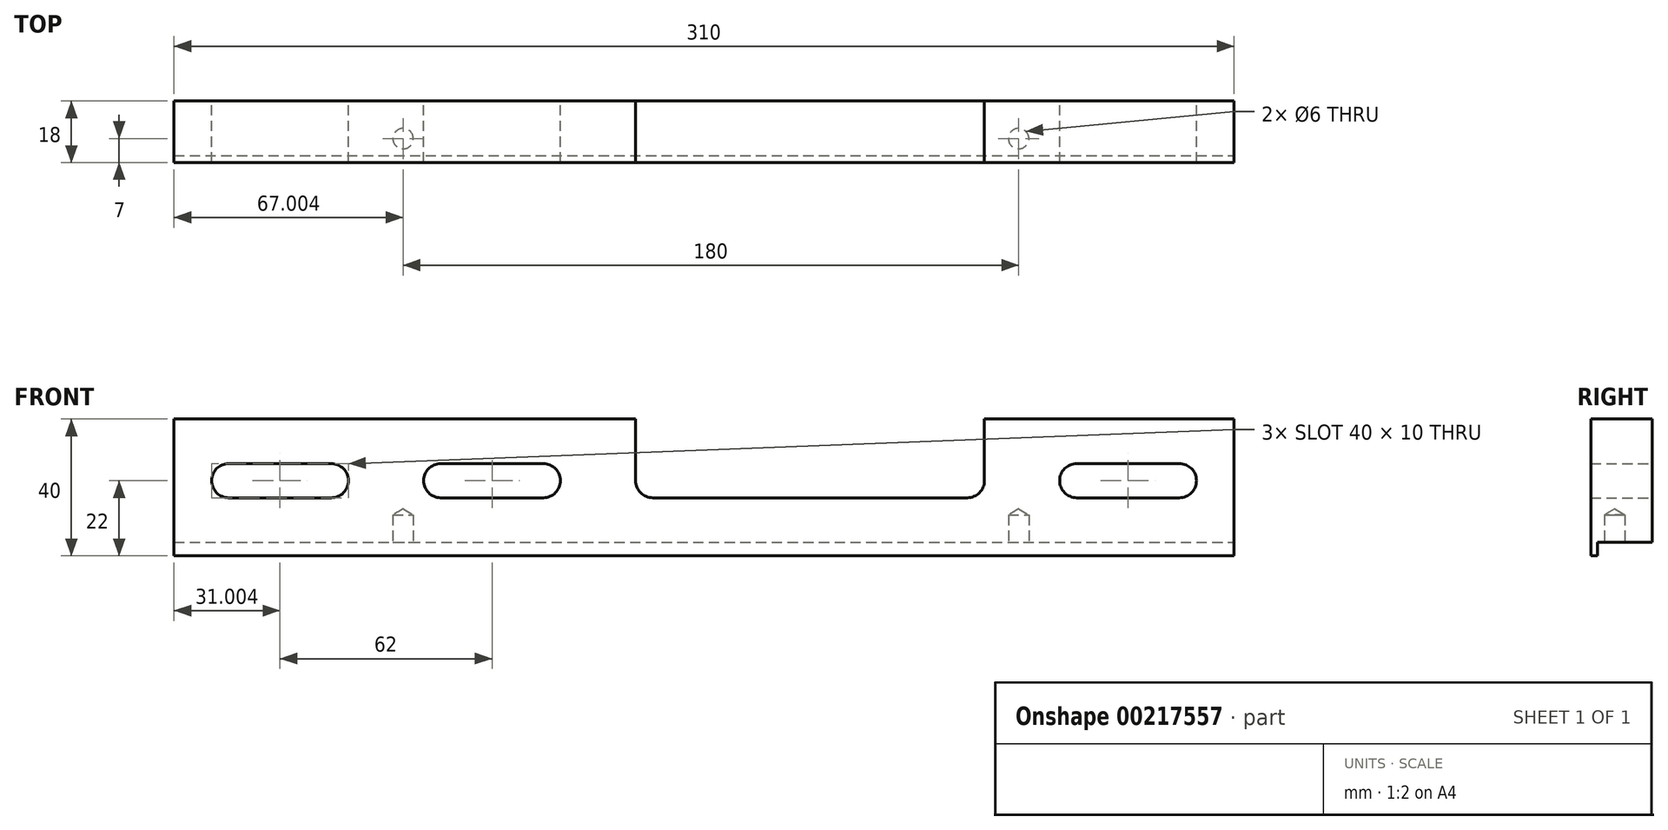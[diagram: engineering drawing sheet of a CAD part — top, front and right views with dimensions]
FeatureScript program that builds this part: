
annotation { "Feature Type Name" : "Feature", "Feature Type Description" : "" }
export const myFeature = defineFeature(function(context is Context, id is Id, definition is map)
    precondition{}
    {
        {
            var Q0;
            Q0=qCreatedBy(makeId("Front.planeOp"),FACE);
            var sketch = newSketch(context, id + "F0", { "sketchPlane" : qUnion([Q0])});
            skPoint(sketch, "E0.endSnap0", {"position": v(-230.99, 42.91) * mm});
            skLineSegment(sketch, "E1", {"start": v(-179.99, 20.91) * mm, "end": v(-489.99, 20.91) * mm});
            skLineSegment(sketch, "E2", {"start": v(-179.99, 20.91) * mm, "end": v(-179.99, 60.91) * mm});
            skLineSegment(sketch, "E3", {"start": v(-179.99, 60.91) * mm, "end": v(-252.99, 60.91) * mm});
            skLineSegment(sketch, "E4", {"start": v(-252.99, 60.91) * mm, "end": v(-252.99, 42.91) * mm});
            skLineSegment(sketch, "E5", {"start": v(-257.99, 37.91) * mm, "end": v(-349.99, 37.91) * mm});
            skLineSegment(sketch, "E6", {"start": v(-354.99, 42.91) * mm, "end": v(-354.99, 60.91) * mm});
            skLineSegment(sketch, "E7", {"start": v(-354.99, 60.91) * mm, "end": v(-489.99, 60.91) * mm});
            skLineSegment(sketch, "E8", {"start": v(-489.99, 60.91) * mm, "end": v(-489.99, 20.91) * mm});
            skLineSegment(sketch, "E9", {"start": v(-473.99, 37.91) * mm, "end": v(-443.99, 37.91) * mm});
            skLineSegment(sketch, "E10", {"start": v(-443.99, 47.91) * mm, "end": v(-473.99, 47.91) * mm});
            skLineSegment(sketch, "E11", {"start": v(-411.99, 37.91) * mm, "end": v(-381.99, 37.91) * mm});
            skLineSegment(sketch, "E12", {"start": v(-381.99, 47.91) * mm, "end": v(-411.99, 47.91) * mm});
            skLineSegment(sketch, "E13", {"start": v(-225.99, 37.91) * mm, "end": v(-195.99, 37.91) * mm});
            skLineSegment(sketch, "E14", {"start": v(-225.99, 47.91) * mm, "end": v(-195.99, 47.91) * mm});
            skArc(sketch, "E15", {"start": v(-195.99, 37.91) * mm, "mid": v(-190.99, 42.91) * mm, "end": v(-195.99, 47.91) * mm});
            skArc(sketch, "E16", {"start": v(-225.99, 47.91) * mm, "mid": v(-230.99, 42.91) * mm, "end": v(-225.99, 37.91) * mm});
            skArc(sketch, "E17", {"start": v(-252.99, 42.91) * mm, "mid": v(-254.45, 39.37) * mm, "end": v(-257.99, 37.91) * mm});
            skArc(sketch, "E18", {"start": v(-354.99, 42.91) * mm, "mid": v(-353.52, 39.37) * mm, "end": v(-349.99, 37.91) * mm});
            skArc(sketch, "E19", {"start": v(-411.99, 37.91) * mm, "mid": v(-416.99, 42.91) * mm, "end": v(-411.99, 47.91) * mm});
            skArc(sketch, "E20", {"start": v(-381.99, 47.91) * mm, "mid": v(-376.99, 42.91) * mm, "end": v(-381.99, 37.91) * mm});
            skArc(sketch, "E21", {"start": v(-473.99, 37.91) * mm, "mid": v(-478.99, 42.91) * mm, "end": v(-473.99, 47.91) * mm});
            skArc(sketch, "E22", {"start": v(-443.99, 47.91) * mm, "mid": v(-438.99, 42.91) * mm, "end": v(-443.99, 37.91) * mm});
            skSolve(sketch);
        }
        {
            var Q0;
            Q0=makeQuery(id+"F0.imprint","IMPRINT",FACE,{"disambiguationData":[TD([[makeQuery(id+"F0.imprint","IMPRINT",EDGE,{"derivedFrom":sQuery(id+"F0.wireOp",EDGE,"E1")}),-1.0]])]});
            extrude(context, id + "F1", {"entities" : qUnion([Q0]), "depth" : 18 * mm});
        }
        {
            var Q0;
            Q0=makeQuery(id+"F1.opExtrude","SWEPT_FACE",FACE,{"disambiguationData":[OSD([sQuery(id+"F0.wireOp",EDGE,"E2")])]});
            var sketch = newSketch(context, id + "F2", { "sketchPlane" : qUnion([Q0])});
            skLineSegment(sketch, "E23", {"start": v(-16, 20.91) * mm, "end": v(-16, 24.91) * mm});
            skLineSegment(sketch, "E24", {"start": v(-16, 24.91) * mm, "end": v(0, 24.91) * mm});
            skLineSegment(sketch, "E25", {"start": v(0, 24.91) * mm, "end": v(0, 20.91) * mm});
            skLineSegment(sketch, "E26", {"start": v(0, 20.91) * mm, "end": v(-16, 20.91) * mm});
            skSolve(sketch);
        }
        {
            var Q0;
            Q0=makeQuery(id+"F2.imprint","IMPRINT",FACE,{"disambiguationData":[TD([[makeQuery(id+"F2.imprint","IMPRINT",EDGE,{"derivedFrom":sQuery(id+"F2.wireOp",EDGE,"E23")}),-1.0]])]});
            extrude(context, id + "F3", {"entities" : qUnion([Q0]), "operationType" : NewBodyOperationType.REMOVE, "oppositeDirection" : true, "depth" : 400 * mm});
        }
        {
            var Q0;
            Q0=makeQuery(id+"F3.boolean.opBoolean","COPY",FACE,{"derivedFrom":makeQuery(id+"F3.opExtrude","SWEPT_FACE",FACE,{"disambiguationData":[OSD([sQuery(id+"F2.wireOp",EDGE,"E24")])]})});
            var sketch = newSketch(context, id + "F4", { "sketchPlane" : qUnion([Q0])});
            skCircle(sketch, "E27", {"center": v(-242.99, 11) * mm, "radius": 3 * mm});
            skCircle(sketch, "E28", {"center": v(-422.99, 11) * mm, "radius": 3 * mm});
            skSolve(sketch);
        }
        {
            var Q0;
            Q0=sQuery(id+"F4.wireOp",VERTEX,"E27.center");
            var Q1;
            Q1=sQuery(id+"F4.wireOp",VERTEX,"E28.center");
            var Q2;
            Q2=makeQuery(id+"F1.opExtrude","SWEPT_BODY",BODY,{"disambiguationData":[OSD([sQuery(id+"F0.wireOp",EDGE,"E1"),sQuery(id+"F0.wireOp",EDGE,"E2"),sQuery(id+"F0.wireOp",EDGE,"E3"),sQuery(id+"F0.wireOp",EDGE,"E4"),sQuery(id+"F0.wireOp",EDGE,"E5"),sQuery(id+"F0.wireOp",EDGE,"E6"),sQuery(id+"F0.wireOp",EDGE,"E7"),sQuery(id+"F0.wireOp",EDGE,"E8"),sQuery(id+"F0.wireOp",EDGE,"E9"),sQuery(id+"F0.wireOp",EDGE,"E10"),sQuery(id+"F0.wireOp",EDGE,"E11"),sQuery(id+"F0.wireOp",EDGE,"E12"),sQuery(id+"F0.wireOp",EDGE,"E13"),sQuery(id+"F0.wireOp",EDGE,"E14"),sQuery(id+"F0.wireOp",EDGE,"E15"),sQuery(id+"F0.wireOp",EDGE,"E16"),sQuery(id+"F0.wireOp",EDGE,"E17"),sQuery(id+"F0.wireOp",EDGE,"E18"),sQuery(id+"F0.wireOp",EDGE,"E19"),sQuery(id+"F0.wireOp",EDGE,"E20"),sQuery(id+"F0.wireOp",EDGE,"E21"),sQuery(id+"F0.wireOp",EDGE,"E22")])]});
            hole(context, id + "F5", {"style" : HoleStyle.SIMPLE, "endStyle" : HoleEndStyle.BLIND, "standardTappedOrClearance" : lookupTablePath({ "standard" : "ISO", "size" : "6", "type" : "Drilled" }), "standardBlindInLast" : lookupTablePath({ "standard" : "ISO", "size" : "6", "type" : "Drilled" }), "holeDiameter" : 6 * mm, "holeDepth" : 8 * mm, "startFromSketch" : true, "locations" : qUnion([Q0, Q1]), "scope" : qUnion([Q2])});
        }
    });
